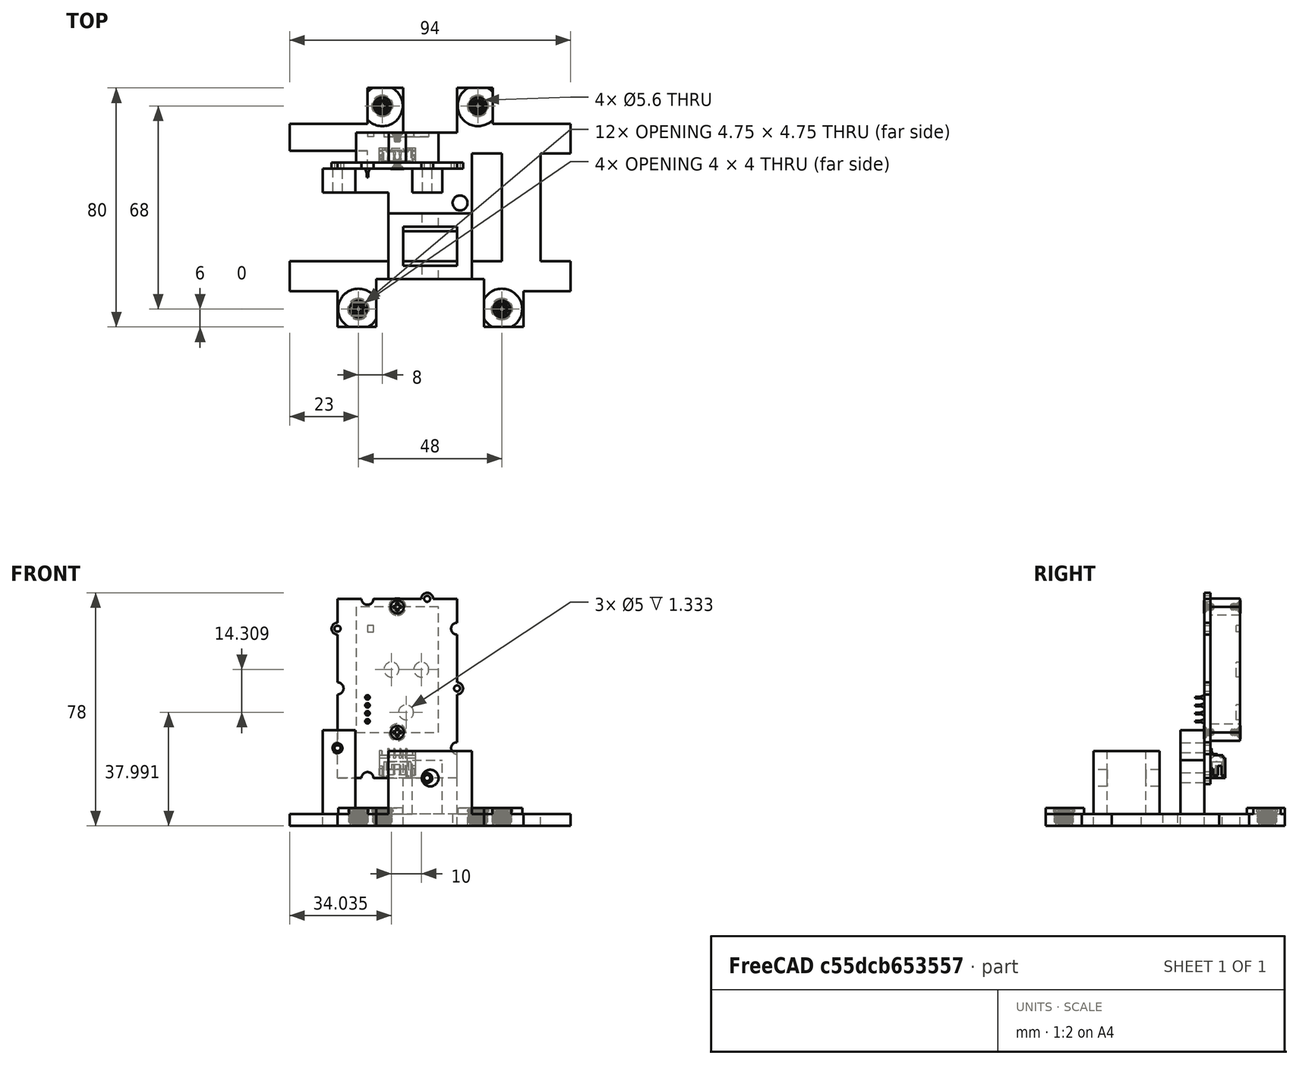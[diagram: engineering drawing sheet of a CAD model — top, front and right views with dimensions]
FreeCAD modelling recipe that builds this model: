
FCSTD DOCUMENT  (FreeCAD 0.20R29177 +233 (Git))
Label: spin07112022
License: All rights reserved
LicenseURL: http://en.wikipedia.org/wiki/All_rights_reserved
objects: Part::Box×23, Part::Cylinder×18, Part::MultiFuse×12, Part::Cut×5, Part::Feature×5
note: 63 computed .brp shape members not serialized (recipe doc carries the construction recipe); baked Part::Feature solids carry a one-line shape summary decoded from their .brp

FEATURE [Part::Cylinder] Cylinder103  label="Cylinder107"
  Angle = 360
  AttacherType = Attacher::AttachEngine3D
  FirstAngle = 0
  Height = 10
  Placement = pos=(63,3,0) rot=(0,0,1;0rad)
  Radius = 2.25
  SecondAngle = 0
FEATURE [Part::Box] Box064  label="base005"
  AttacherType = Attacher::AttachEngine3D
  Height = 4
  Length = 26
  Placement = pos=(-10.25,68,0) rot=(0,0,1;0rad)
  Width = 12
FEATURE [Part::Box] Box060  label="base001"
  AttacherType = Attacher::AttachEngine3D
  Height = 4
  Length = 94
  Width = 80
FEATURE [Part::Box] Box061  label="base002"
  AttacherType = Attacher::AttachEngine3D
  Height = 4
  Length = 26
  Width = 12
FEATURE [Part::Box] Box062  label="base003"
  AttacherType = Attacher::AttachEngine3D
  Height = 4
  Length = 26
  Placement = pos=(68,0,0) rot=(0,0,1;0rad)
  Width = 12
FEATURE [Part::Cylinder] Cylinder104  label="Cylinder103"
  Angle = 360
  AttacherType = Attacher::AttachEngine3D
  FirstAngle = 0
  Height = 10
  Placement = pos=(71,71,0) rot=(0,0,1;0rad)
  Radius = 2.25
  SecondAngle = 0
FEATURE [Part::Cylinder] Cylinder106  label="Cylinder104"
  Angle = 360
  AttacherType = Attacher::AttachEngine3D
  FirstAngle = 0
  Height = 10
  Placement = pos=(23,71,0) rot=(0,0,1;0rad)
  Radius = 2
  SecondAngle = 0
FEATURE [Part::Cylinder] Cylinder105  label="Cylinder108"
  Angle = 360
  AttacherType = Attacher::AttachEngine3D
  FirstAngle = 0
  Height = 10
  Placement = pos=(31,3,0) rot=(0,0,1;0rad)
  Radius = 2.25
  SecondAngle = 0
FEATURE [Part::Box] Box081  label="Cube039"
  AttacherType = Attacher::AttachEngine3D
  Height = 10
  Length = 10
  Placement = pos=(74,26,140) rot=(0,0,1;0rad)
  Width = 36
FEATURE [Part::Box] Box082  label="Cube040"
  AttacherType = Attacher::AttachEngine3D
  Height = 10
  Length = 36
  Placement = pos=(42,1,140) rot=(0,0,1;0rad)
  Width = 19
FEATURE [Part::Box] Box073  label="baseSpineCut"
  AttacherType = Attacher::AttachEngine3D
  Height = 25
  Length = 18
  Placement = pos=(51,26,140) rot=(0,0,1;0rad)
  Width = 10
FEATURE [Part::Cylinder] Cylinder107  label="Cylinder109"
  Angle = 360
  AttacherType = Attacher::AttachEngine3D
  FirstAngle = 0
  Height = 10
  Radius = 1
  SecondAngle = 0
FEATURE [Part::MultiFuse] Fusion123  label="screwIns001"
  Placement = pos=(0,3,0) rot=(0,0,1;0rad)
  Shapes = -> [Cylinder105,Cylinder107,Cylinder103,Cylinder104,Cylinder106]
FEATURE [Part::Box] Box080  label="Cube038"
  AttacherType = Attacher::AttachEngine3D
  Height = 10
  Length = 33
  Placement = pos=(13,26,140) rot=(0,0,1;0rad)
  Width = 23
FEATURE [Part::Box] Box063  label="base004"
  AttacherType = Attacher::AttachEngine3D
  Height = 4
  Length = 26
  Placement = pos=(78,68,0) rot=(0,0,1;0rad)
  Width = 12
FEATURE [Part::MultiFuse] Fusion122
  Shapes = -> [Box064,Box063,Box061,Box062]
FEATURE [Part::Cut] Cut019  label="baseNew"
  Base = -> Box060
  Tool = -> Fusion122
FEATURE [Part::Cut] Cut020  label="baseNew001"
  Base = -> Cut019
  Placement = pos=(107,84,140) rot=(0,0,1;3.14159rad)
  Tool = -> Fusion123
FEATURE [Part::Box] Box083  label="Cube041"
  AttacherType = Attacher::AttachEngine3D
  Height = 25
  Length = 18
  Placement = pos=(51,24.5,144) rot=(0,0,1;0rad)
  Width = 13
FEATURE [Part::Box] Box084  label="Cube042"
  AttacherType = Attacher::AttachEngine3D
  Height = 32
  Length = 40
  Placement = pos=(24,49,140) rot=(0,0,1;0rad)
  Width = 8
FEATURE [Part::Box] Box085  label="Cube043"
  AttacherType = Attacher::AttachEngine3D
  Height = 10
  Length = 15
  Placement = pos=(69,69,140) rot=(0,0,1;1.5708rad)
  Width = 18
FEATURE [Part::Box] Box086  label="baseSpineIn"
  AttacherType = Attacher::AttachEngine3D
  Height = 25
  Length = 28
  Placement = pos=(46,20,140) rot=(0,0,1;0rad)
  Width = 22
FEATURE [Part::Cylinder] Cylinder
  Angle = 360
  AttacherType = Attacher::AttachEngine3D
  FirstAngle = 0
  Height = 50
  Placement = pos=(60,-3,156) rot=(-1,0,0;1.5708rad)
  Radius = 2.8
  SecondAngle = 0
FEATURE [Part::Feature] Feature  label="Seed Grove SCD30"
  Placement = pos=(29,59,156) rot=(0.707107,0,0.707107;3.14159rad)
  shape: bbox 44 x 15.1 x 64 mm, 422 faces, 13 solids (baked)
FEATURE [Part::Cylinder] Cylinder108  label="Cylinder110"
  Angle = 360
  AttacherType = Attacher::AttachEngine3D
  FirstAngle = 0
  Height = 50
  Placement = pos=(80,17,186) rot=(-1,0,0;1.5708rad)
  Radius = 1.65
  SecondAngle = 0
FEATURE [Part::Cylinder] Cylinder109  label="Cylinder111"
  Angle = 360
  AttacherType = Attacher::AttachEngine3D
  FirstAngle = 0
  Height = 50
  Placement = pos=(40,17,166) rot=(-1,0,0;1.5708rad)
  Radius = 1.65
  SecondAngle = 0
FEATURE [Part::Cylinder] Cylinder110  label="Cylinder112"
  Angle = 360
  AttacherType = Attacher::AttachEngine3D
  FirstAngle = 0
  Height = 50
  Placement = pos=(70,17,156) rot=(-1,0,0;1.5708rad)
  Radius = 1.65
  SecondAngle = 0
FEATURE [Part::MultiFuse] Fusion  label="m2Cuts"
  Placement = pos=(-11,30,0) rot=(0,0,1;0rad)
  Shapes = -> [Cylinder108,Cylinder109,Cylinder110]
FEATURE [Part::Box] Box087  label="Cube044"
  AttacherType = Attacher::AttachEngine3D
  Height = 51
  Length = 50
  Placement = pos=(13,49,172) rot=(0,0,1;0rad)
  Width = 8
FEATURE [Part::Box] Box088  label="Cube045"
  AttacherType = Attacher::AttachEngine3D
  Height = 51
  Length = 19
  Placement = pos=(35,49,144) rot=(0,0,1;0rad)
  Width = 8
FEATURE [Part::MultiFuse] Fusion124  label="base"
  Shapes = -> [Cut020,Box084,Box086]
FEATURE [Part::MultiFuse] Fusion125  label="cuts"
  Shapes = -> [Box087,Box088,Fusion,Box085,Box080,Box083,Box082,Box081,Box073,Cylinder]
FEATURE [Part::Box] Box089  label="Cube046"
  AttacherType = Attacher::AttachEngine3D
  Height = 10
  Length = 26
  Placement = pos=(13,57,140) rot=(0,0,1;0rad)
  Width = 6
FEATURE [Part::Feature] Solid  label="m4HeatSet"
  Placement = pos=(36,10,140) rot=(1,0,0;1.5708rad)
  shape: bbox 7.1 x 7.1 x 6.065 mm, 234 faces (baked)
FEATURE [Part::Feature] Solid001  label="m4HeatSet001"
  Placement = pos=(84,10,140) rot=(1,0,0;1.5708rad)
  shape: bbox 7.1 x 7.1 x 6.065 mm, 234 faces (baked)
FEATURE [Part::Feature] Solid002  label="m4HeatSet002"
  Placement = pos=(44,78,140) rot=(1,0,0;1.5708rad)
  shape: bbox 7.1 x 7.1 x 6.065 mm, 234 faces (baked)
FEATURE [Part::Feature] Solid003  label="m4HeatSet003"
  Placement = pos=(76,78,140) rot=(1,0,0;1.5708rad)
  shape: bbox 7.1 x 7.1 x 6.065 mm, 234 faces (baked)
FEATURE [Part::Cylinder] Cylinder111  label="m4HeatSetCut"
  Angle = 360
  AttacherType = Attacher::AttachEngine3D
  FirstAngle = 0
  Height = 10
  Placement = pos=(36,10,140) rot=(0,0,1;0rad)
  Radius = 2.8
  SecondAngle = 0
FEATURE [Part::Cylinder] Cylinder112  label="m4HeatSetCut001"
  Angle = 360
  AttacherType = Attacher::AttachEngine3D
  FirstAngle = 0
  Height = 10
  Placement = pos=(84,10,140) rot=(0,0,1;0rad)
  Radius = 2.8
  SecondAngle = 0
FEATURE [Part::Cylinder] Cylinder113  label="m4HeatSetCut002"
  Angle = 360
  AttacherType = Attacher::AttachEngine3D
  FirstAngle = 0
  Height = 10
  Placement = pos=(76,78,140) rot=(0,0,1;0rad)
  Radius = 2.8
  SecondAngle = 0
FEATURE [Part::Cylinder] Cylinder114  label="m4HeatSetCut003"
  Angle = 360
  AttacherType = Attacher::AttachEngine3D
  FirstAngle = 0
  Height = 10
  Placement = pos=(44,78,140) rot=(0,0,1;0rad)
  Radius = 2.8
  SecondAngle = 0
FEATURE [Part::MultiFuse] Fusion126  label="heatSetCuts"
  Shapes = -> [Cylinder111,Cylinder112,Cylinder113,Cylinder114]
FEATURE [Part::Box] Box091  label="Cube048"
  AttacherType = Attacher::AttachEngine3D
  Height = 10
  Length = 11
  Placement = pos=(13,49,140) rot=(0,0,1;0rad)
  Width = 8
FEATURE [Part::MultiFuse] Fusion127  label="cuts001"
  Shapes = -> [Box091,Fusion126,Box089,Fusion125]
FEATURE [Part::Cylinder] Cylinder115  label="m4HeatSetCut004"
  Angle = 360
  AttacherType = Attacher::AttachEngine3D
  FirstAngle = 0
  Height = 6
  Placement = pos=(36,10,140) rot=(0,0,-1;1.0472rad)
  Radius = 6.8
  SecondAngle = 0
FEATURE [Part::Cylinder] Cylinder116  label="m4HeatSetCut005"
  Angle = 360
  AttacherType = Attacher::AttachEngine3D
  FirstAngle = 0
  Height = 6
  Placement = pos=(84,10,140) rot=(0,0,1;0rad)
  Radius = 6.8
  SecondAngle = 0
FEATURE [Part::Cylinder] Cylinder117  label="m4HeatSetCut006"
  Angle = 360
  AttacherType = Attacher::AttachEngine3D
  FirstAngle = 0
  Height = 6
  Placement = pos=(76,78,140) rot=(0,0,1;0rad)
  Radius = 6.8
  SecondAngle = 0
FEATURE [Part::Cylinder] Cylinder118  label="m4HeatSetCut007"
  Angle = 360
  AttacherType = Attacher::AttachEngine3D
  FirstAngle = 0
  Height = 6
  Placement = pos=(44,78,140) rot=(0,0,1;0rad)
  Radius = 6.8
  SecondAngle = 0
FEATURE [Part::MultiFuse] Fusion128  label="heatSetAddOns"
  Shapes = -> [Cylinder115,Cylinder116,Cylinder117,Cylinder118]
FEATURE [Part::Box] Box092  label="Cube049"
  AttacherType = Attacher::AttachEngine3D
  Height = 10
  Length = 94
  Placement = pos=(13,-4,140) rot=(0,0,1;0rad)
  Width = 8
FEATURE [Part::MultiFuse] Fusion129  label="base006"
  Shapes = -> [Fusion128,Fusion124]
FEATURE [Part::Box] Box093  label="Cube050"
  AttacherType = Attacher::AttachEngine3D
  Height = 10
  Length = 94
  Placement = pos=(13,84,140) rot=(0,0,1;0rad)
  Width = 8
FEATURE [Part::Box] Box094  label="Cube051"
  AttacherType = Attacher::AttachEngine3D
  Height = 10
  Length = 94
  Placement = pos=(89,72,140) rot=(0,0,1;1.5708rad)
  Width = 8
FEATURE [Part::Box] Box095  label="Cube052"
  AttacherType = Attacher::AttachEngine3D
  Height = 10
  Length = 94
  Placement = pos=(39,72,140) rot=(0,0,1;1.5708rad)
  Width = 8
FEATURE [Part::MultiFuse] Fusion130
  Shapes = -> [Box093,Box094,Box095,Box092]
FEATURE [Part::MultiFuse] Fusion131  label="cuts002"
  Shapes = -> [Fusion127,Fusion130]
FEATURE [Part::Box] Box096  label="Cube053"
  AttacherType = Attacher::AttachEngine3D
  Height = 10
  Length = 10
  Placement = pos=(97,26,140) rot=(0,0,1;0rad)
  Width = 36
FEATURE [Part::MultiFuse] Fusion132  label="cuts003"
  Shapes = -> [Fusion131,Box096]
FEATURE [Part::Cut] Cut  label="base007"
  Base = -> Fusion129
  Tool = -> Fusion132
FEATURE [Part::Cylinder] Cylinder119
  Angle = 360
  AttacherType = Attacher::AttachEngine3D
  FirstAngle = 0
  Height = 10
  Placement = pos=(70,45.5,140) rot=(0,0,1;0rad)
  Radius = 2.5
  SecondAngle = 0
FEATURE [Part::Cut] Cut021
  Base = -> Cut
  Tool = -> Cylinder119
FEATURE [Part::Box] Box097  label="Cube054"
  AttacherType = Attacher::AttachEngine3D
  Height = 51
  Length = 19
  Placement = pos=(45,49,162) rot=(0,0,1;0rad)
  Width = 8
FEATURE [Part::Cut] Cut022  label="base008"
  Base = -> Cut021
  Tool = -> Box097
